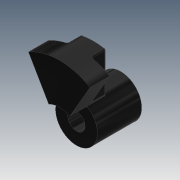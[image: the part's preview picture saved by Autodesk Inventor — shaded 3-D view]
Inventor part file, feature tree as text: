
AUTODESK INVENTOR PART (.ipt)
format: ipt  version: 2017 (Build 210142000, 142)  size: 139,776 bytes
history: native  units: mm
features: sketch x3, extrude x2, other x1, revolve x1, fillet x1, projected_geometry x1
ambient origin geometry x8: Origin, YZ Plane, XZ Plane, XY Plane, X Axis, Y Axis, Z Axis, Center Point
bodies: Body1 (feature_tree)
feature tree (9):
  other  "Твердое тело1"
  revolve  "Вращение1"
  extrude  "Выдавливание1"  Depth=5.0mm
  extrude  "Выдавливание2"  Depth=1.4mm
  fillet  "Сопряжение1"  Radius=3.4mm
  sketch  "Эскиз1"
  sketch  "Эскиз2"
  sketch  "Эскиз3"
  projected_geometry  "Спроецированная петля1"
